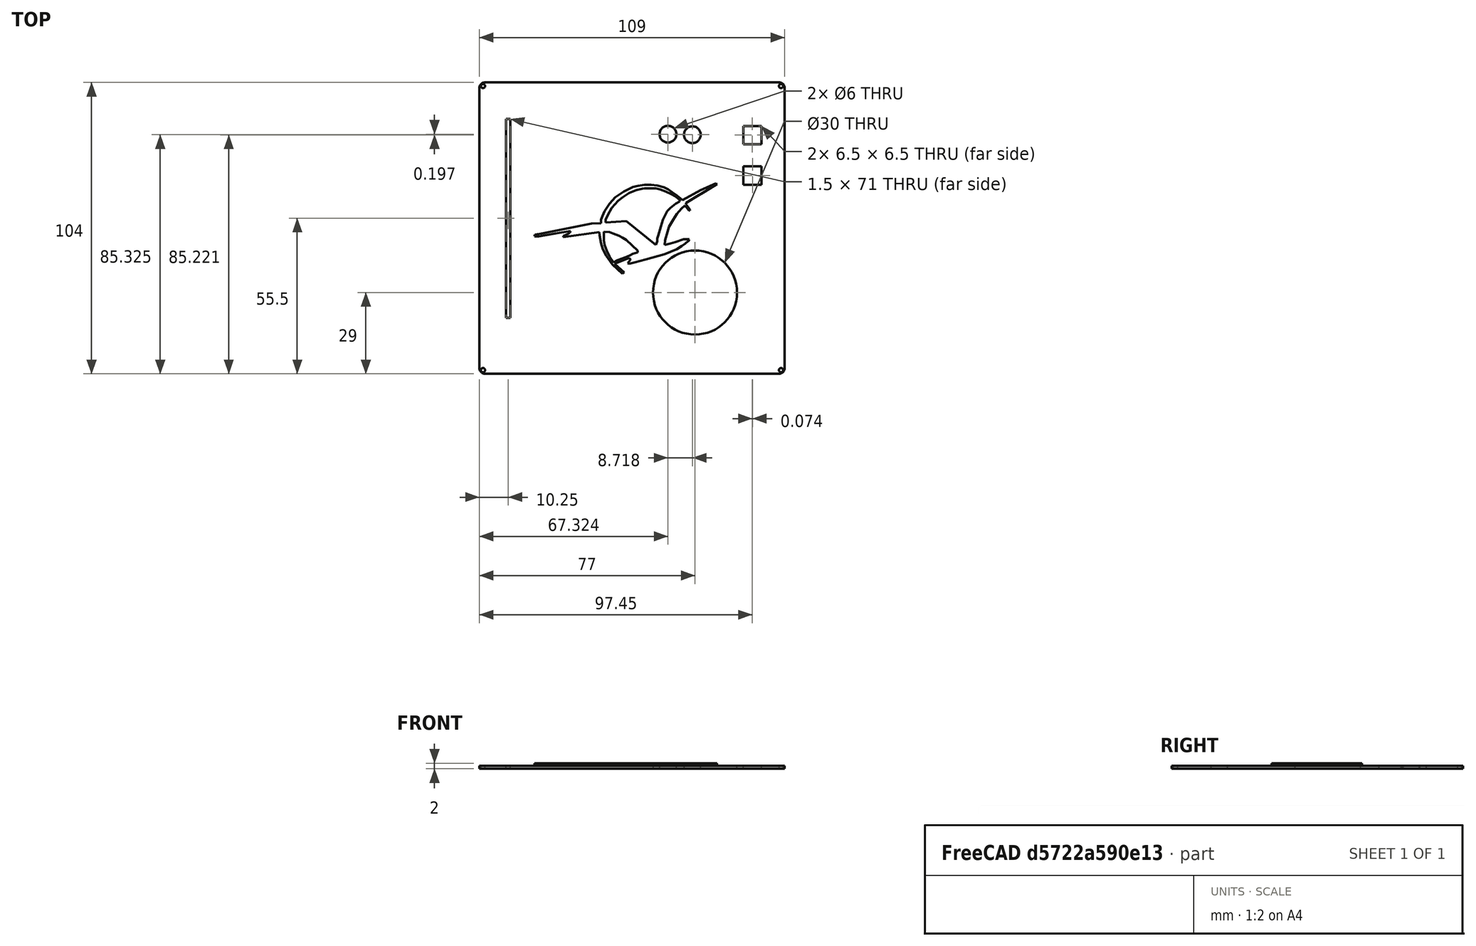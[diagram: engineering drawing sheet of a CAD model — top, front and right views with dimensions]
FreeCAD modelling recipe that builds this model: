
FCSTD DOCUMENT  (FreeCAD 2024.1R35694 (Git))
Label: kryshka
License: All rights reserved
LicenseURL: https://en.wikipedia.org/wiki/All_rights_reserved
objects: Sketcher::SketchObject×3, PartDesign::Pad×2, Image::ImagePlane×1, PartDesign::Body×1, App::MeasureDistance×1
note: 8 computed .brp shape members not serialized (recipe doc carries the construction recipe); baked Part::Feature solids carry a one-line shape summary decoded from their .brp

FEATURE [Sketcher::SketchObject] Sketch
  FullyConstrained = false
  MapMode = 5
  Support = -> [XY_Plane]
  sketch-geometry (29):
    g0: LineSegment StartX=-54.5 StartY=50 StartZ=0 EndX=-54.5 EndY=-50 EndZ=0
    g1: LineSegment StartX=-52.5 StartY=-52 StartZ=0 EndX=52.5 EndY=-52 EndZ=0
    g2: LineSegment StartX=54.5 StartY=-50 StartZ=0 EndX=54.5 EndY=50 EndZ=0
    g3: LineSegment StartX=52.5 StartY=52 StartZ=0 EndX=-52.5 EndY=52 EndZ=0
    g4: ArcOfCircle CenterX=-52.5 CenterY=50 CenterZ=0 NormalX=0 NormalY=0 NormalZ=1 AngleXU=0 Radius=2 StartAngle=1.5708 EndAngle=3.14159
    g5: ArcOfCircle CenterX=-52.5 CenterY=-50 CenterZ=0 NormalX=0 NormalY=0 NormalZ=1 AngleXU=0 Radius=2 StartAngle=3.14159 EndAngle=4.71239
    g6: ArcOfCircle CenterX=52.5 CenterY=-50 CenterZ=0 NormalX=0 NormalY=0 NormalZ=1 AngleXU=0 Radius=2 StartAngle=4.71239 EndAngle=6.28319
    g7: ArcOfCircle CenterX=52.5 CenterY=50 CenterZ=0 NormalX=0 NormalY=0 NormalZ=1 AngleXU=0 Radius=2 StartAngle=-1.8e-15 EndAngle=1.5708
    g8: GeomPoint X=-54.5 Y=52 Z=0
    g9: GeomPoint X=54.5 Y=-52 Z=0
    g10: Circle CenterX=-53.2 CenterY=50.7 CenterZ=0 NormalX=0 NormalY=0 NormalZ=1 AngleXU=0 Radius=0.75
    g11: Circle CenterX=-53.2 CenterY=-50.7 CenterZ=0 NormalX=0 NormalY=0 NormalZ=1 AngleXU=0 Radius=0.75
    g12: Circle CenterX=53.2 CenterY=-50.7 CenterZ=0 NormalX=0 NormalY=0 NormalZ=1 AngleXU=0 Radius=0.75
    g13: Circle CenterX=53.2 CenterY=50.7 CenterZ=0 NormalX=0 NormalY=0 NormalZ=1 AngleXU=0 Radius=0.75
    g14: LineSegment StartX=-45 StartY=39 StartZ=0 EndX=-45 EndY=-32 EndZ=0
    g15: LineSegment StartX=-45 StartY=-32 StartZ=0 EndX=-43.5 EndY=-32 EndZ=0
    g16: LineSegment StartX=-43.5 StartY=-32 StartZ=0 EndX=-43.5 EndY=39 EndZ=0
    g17: LineSegment StartX=-43.5 StartY=39 StartZ=0 EndX=-45 EndY=39 EndZ=0
    g18: Circle CenterX=22.5 CenterY=-23 CenterZ=0 NormalX=0 NormalY=0 NormalZ=1 AngleXU=0 Radius=15
    g19: Circle CenterX=12.8244 CenterY=33.5216 CenterZ=0 NormalX=0 NormalY=0 NormalZ=1 AngleXU=0 Radius=3
    g20: Circle CenterX=21.5427 CenterY=33.3249 CenterZ=0 NormalX=0 NormalY=0 NormalZ=1 AngleXU=0 Radius=3
    g21: LineSegment StartX=39.7743 StartY=22.006 StartZ=0 EndX=39.7743 EndY=15.506 EndZ=0
    g22: LineSegment StartX=39.7743 StartY=15.506 StartZ=0 EndX=46.2743 EndY=15.506 EndZ=0
    g23: LineSegment StartX=46.2743 StartY=15.506 StartZ=0 EndX=46.2743 EndY=22.006 EndZ=0
    g24: LineSegment StartX=46.2743 StartY=22.006 StartZ=0 EndX=39.7743 EndY=22.006 EndZ=0
    g25: LineSegment StartX=39.7003 StartY=36.4714 StartZ=0 EndX=39.7003 EndY=29.9714 EndZ=0
    g26: LineSegment StartX=39.7003 StartY=29.9714 StartZ=0 EndX=46.2003 EndY=29.9714 EndZ=0
    g27: LineSegment StartX=46.2003 StartY=29.9714 StartZ=0 EndX=46.2003 EndY=36.4714 EndZ=0
    g28: LineSegment StartX=46.2003 StartY=36.4714 StartZ=0 EndX=39.7003 EndY=36.4714 EndZ=0
  constraints (72):
    c: Tangent(g0,g4) = -1.5708
    c: Tangent(g0,g5) = -1.5708
    c: Tangent(g1,g5) = -1.5708
    c: Tangent(g1,g6) = -1.5708
    c: Tangent(g2,g6) = -1.5708
    c: Tangent(g2,g7) = -1.5708
    c: Tangent(g3,g7) = -1.5708
    c: Tangent(g3,g4) = -1.5708
    c: Vertical(g0)
    c: Vertical(g2)
    c: Horizontal(g1)
    c: Horizontal(g3)
    c: Equal(g4,g5)
    c: Equal(g5,g6)
    c: Equal(g6,g7)
    c: PointOnObject(g8,g0)
    c: PointOnObject(g8,g3)
    c: PointOnObject(g9,g1)
    c: PointOnObject(g9,g2)
    c: Distance(g0,g2) = 109
    c: Distance(g1,g3) = 104
    c: Radius(g5) = 2
    c: Symmetric(g8,g9,g-1)
    c: Radius(g10) = 0.75
    c: DistanceY(g4,g10) = 0.7
    c: DistanceX(g10,g4) = 0.7
    c: Radius(g11) = 0.75
    c: DistanceX(g11,g5) = 0.7
    c: DistanceY(g11,g5) = 0.7
    c: Radius(g12) = 0.75
    c: DistanceY(g12,g6) = 0.7
    c: DistanceX(g6,g12) = 0.7
    c: Radius(g13) = 0.75
    c: DistanceY(g7,g13) = 0.7
    c: DistanceX(g7,g13) = 0.7
    c: Coincident(g14,g15)
    c: Coincident(g15,g16)
    c: Coincident(g16,g17)
    c: Coincident(g17,g14)
    c: Vertical(g14)
    c: Vertical(g16)
    c: Horizontal(g15)
    c: Horizontal(g17)
    c: Distance(g14,g16) = 1.5
    c: Distance(g15,g17) = 71
    c: DistanceX(g0,g14) = 9.5
    c: DistanceY(g14,g3) = 13
    c: Radius(g18) = 15
    c: DistanceX(g18,g2) = 32
    c: DistanceY(g9,g18) = 29
    c: Radius(g19) = 3
    c: Radius(g20) = 3
    c: Coincident(g21,g22)
    c: Coincident(g22,g23)
    c: Coincident(g23,g24)
    c: Coincident(g24,g21)
    c: Vertical(g21)
    c: Vertical(g23)
    c: Horizontal(g22)
    c: Horizontal(g24)
    c: Distance(g21,g23) = 6.5
    c: Distance(g22,g24) = 6.5
    c: Coincident(g25,g26)
    c: Coincident(g26,g27)
    c: Coincident(g27,g28)
    c: Coincident(g28,g25)
    c: Vertical(g25)
    c: Vertical(g27)
    c: Horizontal(g26)
    c: Horizontal(g28)
    c: Distance(g25,g27) = 6.5
    c: Distance(g26,g28) = 6.5
FEATURE [PartDesign::Pad] Pad
  Direction = (0,0,1)
  Length = 1
  Length2 = 10
  Profile = -> Sketch
  ReferenceAxis = -> Sketch [N_Axis]
  Refine = true
  Type = 0
FEATURE [Sketcher::SketchObject] Sketch001
  FullyConstrained = true
  MapMode = 5
  Placement = pos=(39.7003,0,0) rot=(0.57735,0.57735,0.57735;2.0944rad)
  Support = -> [Pad]
FEATURE [Image::ImagePlane] rt
  XSize = 78.3069
  YSize = 44.9735
FEATURE [Sketcher::SketchObject] Sketch002
  FullyConstrained = false
  MapMode = 5
  Support = -> [XY_Plane]
  sketch-geometry (121):
    g0: LineSegment StartX=-34.7733 StartY=-3 StartZ=0 EndX=-34.7499 EndY=-2.33713 EndZ=0
    g1: LineSegment StartX=-34.7499 StartY=-2.33713 StartZ=0 EndX=-32.2664 EndY=-2 EndZ=0
    g2: LineSegment StartX=-32.2664 StartY=-2 StartZ=0 EndX=-14.5219 EndY=1.61821 EndZ=0
    g3: LineSegment StartX=-14.5219 StartY=1.61821 StartZ=0 EndX=-11 EndY=1.79215 EndZ=0
    g4: LineSegment StartX=-11 StartY=1.79215 StartZ=0 EndX=-11 EndY=3 EndZ=0
    g5: LineSegment StartX=-11 StartY=3 StartZ=0 EndX=-10.5907 EndY=4.26218 EndZ=0
    g6: LineSegment StartX=-10.5907 StartY=4.26218 StartZ=0 EndX=-9.75577 EndY=6 EndZ=0
    g7: LineSegment StartX=-9.75577 StartY=6 StartZ=0 EndX=-8 EndY=8.77106 EndZ=0
    g8: LineSegment StartX=-8 StartY=8.77106 StartZ=0 EndX=-6 EndY=11 EndZ=0
    g9: LineSegment StartX=-6 StartY=11 StartZ=0 EndX=-3 EndY=13 EndZ=0
    g10: LineSegment StartX=-3 StartY=13 StartZ=0 EndX=0.374559 EndY=14.714 EndZ=0
    g11: LineSegment StartX=0.374559 StartY=14.714 StartZ=0 EndX=2.2 EndY=15.1 EndZ=0
    g12: LineSegment StartX=2.2 StartY=15.1 StartZ=0 EndX=4.45571 EndY=15.4013 EndZ=0
    g13: LineSegment StartX=4.45571 StartY=15.4013 StartZ=0 EndX=6.78659 EndY=15.4013 EndZ=0
    g14: LineSegment StartX=6.78659 StartY=15.4013 StartZ=0 EndX=9 EndY=15.2221 EndZ=0
    g15: LineSegment StartX=9 StartY=15.2221 StartZ=0 EndX=11.4375 EndY=14.5437 EndZ=0
    g16: LineSegment StartX=11.4375 StartY=14.5437 StartZ=0 EndX=13 EndY=13.7546 EndZ=0
    g17: LineSegment StartX=13 StartY=13.7546 StartZ=0 EndX=14.3855 EndY=12.7719 EndZ=0
    g18: LineSegment StartX=14.3855 StartY=12.7719 StartZ=0 EndX=16 EndY=11.6183 EndZ=0
    g19: LineSegment StartX=16 StartY=11.6183 StartZ=0 EndX=18 EndY=10 EndZ=0
    g20: LineSegment StartX=18 StartY=10 StartZ=0 EndX=24.5463 EndY=13.5843 EndZ=0
    g21: LineSegment StartX=24.5463 StartY=13.5843 StartZ=0 EndX=30 EndY=16 EndZ=0
    g22: LineSegment StartX=30 StartY=16 StartZ=0 EndX=30.2896 EndY=15.7063 EndZ=0
    g23: LineSegment StartX=30.2896 StartY=15.7063 StartZ=0 EndX=26 EndY=13 EndZ=0
    g24: LineSegment StartX=26 StartY=13 StartZ=0 EndX=22.6257 EndY=11 EndZ=0
    g25: LineSegment StartX=22.6257 StartY=11 StartZ=0 EndX=19.3042 EndY=9 EndZ=0
    g26: LineSegment StartX=19.3042 StartY=9 StartZ=0 EndX=19.3042 EndY=8.49227 EndZ=0
    g27: LineSegment StartX=19.3042 StartY=8.49227 StartZ=0 EndX=20.6795 EndY=6.52009 EndZ=0
    g28: LineSegment StartX=20.6795 StartY=6.52009 StartZ=0 EndX=20.7055 EndY=6.2606 EndZ=0
    g29: LineSegment StartX=20.7055 StartY=6.2606 StartZ=0 EndX=20.2903 EndY=6.3125 EndZ=0
    g30: LineSegment StartX=20.2903 StartY=6.3125 StartZ=0 EndX=18.8598 EndY=8.1 EndZ=0
    g31: LineSegment StartX=18.8598 StartY=8.1 StartZ=0 EndX=17.6926 EndY=7 EndZ=0
    g32: LineSegment StartX=17.6926 StartY=7 StartZ=0 EndX=16 EndY=5 EndZ=0
    g33: LineSegment StartX=16 StartY=5 StartZ=0 EndX=14.7084 EndY=3 EndZ=0
    g34: LineSegment StartX=14.7084 StartY=3 StartZ=0 EndX=13.2552 EndY=0.51859 EndZ=0
    g35: LineSegment StartX=13.2552 StartY=0.51859 StartZ=0 EndX=12.6673 EndY=-1.26122 EndZ=0
    g36: LineSegment StartX=12.6673 StartY=-1.26122 StartZ=0 EndX=11.7962 EndY=-4.36312 EndZ=0
    g37: LineSegment StartX=11.7962 StartY=-4.36312 StartZ=0 EndX=11.6475 EndY=-6 EndZ=0
    g38: LineSegment StartX=11.6475 StartY=-6 StartZ=0 EndX=13.7508 EndY=-5.55289 EndZ=0
    g39: LineSegment StartX=13.7508 StartY=-5.55289 StartZ=0 EndX=15.4292 EndY=-5 EndZ=0
    g40: LineSegment StartX=15.4292 StartY=-5 StartZ=0 EndX=18.4249 EndY=-4 EndZ=0
    g41: LineSegment StartX=18.4249 StartY=-4 StartZ=0 EndX=20.4433 EndY=-4 EndZ=0
    g42: LineSegment StartX=20.4433 StartY=-4 StartZ=0 EndX=20 EndY=-4.55433 EndZ=0
    g43: LineSegment StartX=20 StartY=-4.55433 StartZ=0 EndX=19 EndY=-5.4679 EndZ=0
    g44: LineSegment StartX=19 StartY=-5.4679 StartZ=0 EndX=17.7932 EndY=-6.43095 EndZ=0
    g45: LineSegment StartX=17.7932 StartY=-6.43095 StartZ=0 EndX=16 EndY=-7.47463 EndZ=0
    g46: LineSegment StartX=16 StartY=-7.47463 StartZ=0 EndX=11.6181 EndY=-9.30106 EndZ=0
    g47: LineSegment StartX=11.6181 StartY=-9.30106 StartZ=0 EndX=4.78203 EndY=-11.2493 EndZ=0
    g48: LineSegment StartX=4.78203 StartY=-11.2493 StartZ=0 EndX=1 EndY=-12.2364 EndZ=0
    g49: LineSegment StartX=1 StartY=-12.2364 StartZ=0 EndX=-1 EndY=-12.793 EndZ=0
    g50: LineSegment StartX=-1 StartY=-12.793 StartZ=0 EndX=-1.5477 EndY=-12.4625 EndZ=0
    g51: LineSegment StartX=-1.5477 StartY=-12.4625 StartZ=0 EndX=-0.623532 EndY=-11.4271 EndZ=0
    g52: LineSegment StartX=-0.623532 StartY=-11.4271 StartZ=0 EndX=-0.6 EndY=-10.9 EndZ=0
    g53: LineSegment StartX=-0.6 StartY=-10.9 StartZ=0 EndX=-1 EndY=-10.7451 EndZ=0
    g54: LineSegment StartX=-1 StartY=-10.7451 StartZ=0 EndX=-1.8 EndY=-10.9252 EndZ=0
    g55: LineSegment StartX=-1.8 StartY=-10.9252 StartZ=0 EndX=-6.24816 EndY=-12.6962 EndZ=0
    g56: LineSegment StartX=-6.24816 StartY=-12.6962 StartZ=0 EndX=-2.83824 EndY=-15.8401 EndZ=0
    g57: LineSegment StartX=-2.83824 StartY=-15.8401 StartZ=0 EndX=-3.4 EndY=-16.2562 EndZ=0
    g58: LineSegment StartX=-3.4 StartY=-16.2562 StartZ=0 EndX=-7 EndY=-13 EndZ=0
    g59: LineSegment StartX=-7 StartY=-13 StartZ=0 EndX=-9.22125 EndY=-10 EndZ=0
    g60: LineSegment StartX=-9.22125 StartY=-10 StartZ=0 EndX=-10.3943 EndY=-7.51802 EndZ=0
    g61: LineSegment StartX=-10.3943 StartY=-7.51802 StartZ=0 EndX=-11 EndY=-5.35344 EndZ=0
    g62: LineSegment StartX=-11 StartY=-5.35344 StartZ=0 EndX=-11.5843 EndY=-2.59002 EndZ=0
    g63: LineSegment StartX=-11.5843 StartY=-2.59002 StartZ=0 EndX=-11.666 EndY=-1.38904 EndZ=0
    g64: LineSegment StartX=-11.666 StartY=-1.38904 StartZ=0 EndX=-24.5219 EndY=-3.23781 EndZ=0
    g65: LineSegment StartX=-24.5219 StartY=-3.23781 StartZ=0 EndX=-24.5503 EndY=-2.78208 EndZ=0
    g66: LineSegment StartX=-24.5503 StartY=-2.78208 StartZ=0 EndX=-23.4253 EndY=-2.36907 EndZ=0
    g67: LineSegment StartX=-23.4253 StartY=-2.36907 StartZ=0 EndX=-22.2147 EndY=-1.65699 EndZ=0
    g68: LineSegment StartX=-22.2147 StartY=-1.65699 StartZ=0 EndX=-22 EndY=-1 EndZ=0
    g69: LineSegment StartX=-22 StartY=-1 StartZ=0 EndX=-27.4592 EndY=-2 EndZ=0
    g70: LineSegment StartX=-27.4592 StartY=-2 StartZ=0 EndX=-33.3013 EndY=-3 EndZ=0
    g71: LineSegment StartX=-33.3013 StartY=-3 StartZ=0 EndX=-34.7733 EndY=-3 EndZ=0
    g72: LineSegment StartX=-10 StartY=-1.33522 StartZ=0 EndX=-8 EndY=-1.40755 EndZ=0
    g73: LineSegment StartX=-8 StartY=-1.40755 StartZ=0 EndX=-6.69036 EndY=-2 EndZ=0
    g74: LineSegment StartX=-6.69036 StartY=-2 StartZ=0 EndX=-4.76445 EndY=-2.73196 EndZ=0
    g75: LineSegment StartX=-4.76445 StartY=-2.73196 StartZ=0 EndX=-3.31128 EndY=-3.51045 EndZ=0
    g76: LineSegment StartX=-3.31128 StartY=-3.51045 StartZ=0 EndX=-2 EndY=-4.28894 EndZ=0
    g77: LineSegment StartX=-2 StartY=-4.28894 StartZ=0 EndX=2 EndY=-8 EndZ=0
    g78: LineSegment StartX=2 StartY=-8 StartZ=0 EndX=2 EndY=-8.46683 EndZ=0
    g79: LineSegment StartX=2 StartY=-8.46683 StartZ=0 EndX=2 EndY=-8.70038 EndZ=0
    g80: LineSegment StartX=2 StartY=-8.70038 StartZ=0 EndX=0.29573 EndY=-9.24532 EndZ=0
    g81: LineSegment StartX=0.29573 StartY=-9.24532 StartZ=0 EndX=-0.664407 EndY=-9.68647 EndZ=0
    g82: LineSegment StartX=-0.664407 StartY=-9.68647 StartZ=0 EndX=-2 EndY=-10.2833 EndZ=0
    g83: LineSegment StartX=-2 StartY=-10.2833 StartZ=0 EndX=-5.2575 EndY=-11.5289 EndZ=0
    g84: LineSegment StartX=-5.2575 StartY=-11.5289 StartZ=0 EndX=-6.63321 EndY=-12.2534 EndZ=0
    g85: LineSegment StartX=-6.63321 StartY=-12.2534 StartZ=0 EndX=-8 EndY=-10.2487 EndZ=0
    g86: LineSegment StartX=-8 StartY=-10.2487 StartZ=0 EndX=-9 EndY=-8 EndZ=0
    g87: LineSegment StartX=-9 StartY=-8 StartZ=0 EndX=-9.78238 EndY=-6 EndZ=0
    g88: LineSegment StartX=-9.78238 StartY=-6 StartZ=0 EndX=-10 EndY=-4.41003 EndZ=0
    g89: LineSegment StartX=-10 StartY=-4.41003 StartZ=0 EndX=-10 EndY=-1.33522 EndZ=0
    g90: LineSegment StartX=-9.47686 StartY=2 StartZ=0 EndX=-9.47686 EndY=3 EndZ=0
    g91: LineSegment StartX=-9.47686 StartY=3 StartZ=0 EndX=-8.70385 EndY=4.62033 EndZ=0
    g92: LineSegment StartX=-8.70385 StartY=4.62033 StartZ=0 EndX=-7.23514 EndY=7.23705 EndZ=0
    g93: LineSegment StartX=-7.23514 StartY=7.23705 StartZ=0 EndX=-5 EndY=9.69777 EndZ=0
    g94: LineSegment StartX=-5 StartY=9.69777 StartZ=0 EndX=-3.36412 EndY=11 EndZ=0
    g95: LineSegment StartX=-3.36412 StartY=11 StartZ=0 EndX=-1 EndY=12.5331 EndZ=0
    g96: LineSegment StartX=-1 StartY=12.5331 StartZ=0 EndX=1.56882 EndY=13.5121 EndZ=0
    g97: LineSegment StartX=1.56882 StartY=13.5121 StartZ=0 EndX=3.64807 EndY=14 EndZ=0
    g98: LineSegment StartX=3.64807 StartY=14 StartZ=0 EndX=4.4 EndY=14.1486 EndZ=0
    g99: LineSegment StartX=4.4 StartY=14.1486 StartZ=0 EndX=7.4 EndY=14.1486 EndZ=0
    g100: LineSegment StartX=7.4 StartY=14.1486 StartZ=0 EndX=8.46425 EndY=14.1486 EndZ=0
    g101: LineSegment StartX=8.46425 StartY=14.1486 StartZ=0 EndX=10 EndY=13.748 EndZ=0
    g102: LineSegment StartX=10 StartY=13.748 StartZ=0 EndX=11 EndY=13.4692 EndZ=0
    g103: LineSegment StartX=11 StartY=13.4692 StartZ=0 EndX=12.048 EndY=13.1 EndZ=0
    g104: LineSegment StartX=12.048 StartY=13.1 StartZ=0 EndX=13.9539 EndY=12.1727 EndZ=0
    g105: LineSegment StartX=13.9539 StartY=12.1727 StartZ=0 EndX=15.3 EndY=11.3467 EndZ=0
    g106: LineSegment StartX=15.3 StartY=11.3467 StartZ=0 EndX=17 EndY=10.1705 EndZ=0
    g107: LineSegment StartX=17 StartY=10.1705 StartZ=0 EndX=17.033 EndY=9.44742 EndZ=0
    g108: LineSegment StartX=17.033 StartY=9.44742 StartZ=0 EndX=15.5751 EndY=8.67393 EndZ=0
    g109: LineSegment StartX=15.5751 StartY=8.67393 StartZ=0 EndX=13.727 EndY=7.2256 EndZ=0
    g110: LineSegment StartX=13.727 StartY=7.2256 StartZ=0 EndX=13 EndY=6.482 EndZ=0
    g111: LineSegment StartX=13 StartY=6.482 StartZ=0 EndX=12.6009 EndY=6 EndZ=0
    g112: LineSegment StartX=12.6009 StartY=6 StartZ=0 EndX=12 EndY=5 EndZ=0
    g113: LineSegment StartX=12 StartY=5 StartZ=0 EndX=11 EndY=3 EndZ=0
    g114: LineSegment StartX=11 StartY=3 StartZ=0 EndX=10.2202 EndY=0.508264 EndZ=0
    g115: LineSegment StartX=10.2202 StartY=0.508264 StartZ=0 EndX=9.36427 EndY=-2.641 EndZ=0
    g116: LineSegment StartX=9.36427 StartY=-2.641 StartZ=0 EndX=9 EndY=-3.78279 EndZ=0
    g117: LineSegment StartX=9 StartY=-3.78279 StartZ=0 EndX=9 EndY=-4.71698 EndZ=0
    g118: LineSegment StartX=9 StartY=-4.71698 StartZ=0 EndX=8.54919 EndY=-6 EndZ=0
    g119: LineSegment StartX=8.54919 StartY=-6 StartZ=0 EndX=-2 EndY=2.54303 EndZ=0
    g120: LineSegment StartX=-2 StartY=2.54303 StartZ=0 EndX=-9.47686 EndY=2 EndZ=0
  constraints (133):
    c: Coincident(g0,g1)
    c: Coincident(g1,g2)
    c: Coincident(g2,g3)
    c: Coincident(g3,g4)
    c: Vertical(g4)
    c: Coincident(g4,g5)
    c: Coincident(g5,g6)
    c: Coincident(g6,g7)
    c: Coincident(g7,g8)
    c: Coincident(g8,g9)
    c: Coincident(g9,g10)
    c: Coincident(g10,g11)
    c: Coincident(g11,g12)
    c: Coincident(g12,g13)
    c: Horizontal(g13)
    c: Coincident(g13,g14)
    c: Coincident(g14,g15)
    c: Coincident(g15,g16)
    c: Coincident(g16,g17)
    c: Coincident(g17,g18)
    c: Coincident(g18,g19)
    c: Coincident(g19,g20)
    c: Coincident(g20,g21)
    c: Coincident(g21,g22)
    c: Coincident(g22,g23)
    c: Coincident(g23,g24)
    c: Coincident(g24,g25)
    c: Coincident(g25,g26)
    c: Vertical(g26)
    c: Coincident(g26,g27)
    c: Coincident(g27,g28)
    c: Coincident(g28,g29)
    c: Coincident(g29,g30)
    c: Coincident(g30,g31)
    c: Coincident(g31,g32)
    c: Coincident(g32,g33)
    c: Coincident(g33,g34)
    c: Coincident(g34,g35)
    c: Coincident(g35,g36)
    c: Coincident(g36,g37)
    c: Coincident(g37,g38)
    c: Coincident(g38,g39)
    c: Coincident(g39,g40)
    c: Coincident(g40,g41)
    c: Horizontal(g41)
    c: Coincident(g41,g42)
    c: Coincident(g42,g43)
    c: Coincident(g43,g44)
    c: Coincident(g44,g45)
    c: Coincident(g45,g46)
    c: Coincident(g46,g47)
    c: Coincident(g47,g48)
    c: Coincident(g48,g49)
    c: Coincident(g49,g50)
    c: Coincident(g50,g51)
    c: Coincident(g51,g52)
    c: Coincident(g52,g53)
    c: Coincident(g53,g54)
    c: Coincident(g54,g55)
    c: Coincident(g55,g56)
    c: Coincident(g56,g57)
    c: Coincident(g57,g58)
    c: Coincident(g58,g59)
    c: Coincident(g59,g60)
    c: Coincident(g60,g61)
    c: Coincident(g61,g62)
    c: Coincident(g62,g63)
    c: Coincident(g63,g64)
    c: Coincident(g64,g65)
    c: Coincident(g65,g66)
    c: Coincident(g66,g67)
    c: Coincident(g67,g68)
    c: Coincident(g68,g69)
    c: Coincident(g69,g70)
    c: Coincident(g70,g71)
    c: Coincident(g71,g0)
    c: Horizontal(g71)
    c: Coincident(g72,g73)
    c: Coincident(g73,g74)
    c: Coincident(g74,g75)
    c: Coincident(g75,g76)
    c: Coincident(g76,g77)
    c: Coincident(g77,g78)
    c: Vertical(g78)
    c: Coincident(g78,g79)
    c: Vertical(g79)
    c: Coincident(g79,g80)
    c: Coincident(g80,g81)
    c: Coincident(g81,g82)
    c: Coincident(g82,g83)
    c: Coincident(g83,g84)
    c: Coincident(g84,g85)
    c: Coincident(g85,g86)
    c: Coincident(g86,g87)
    c: Coincident(g87,g88)
    c: Coincident(g88,g89)
    c: Coincident(g89,g72)
    c: Vertical(g89)
    c: Vertical(g90)
    c: Coincident(g90,g91)
    c: Coincident(g91,g92)
    c: Coincident(g92,g93)
    c: Coincident(g93,g94)
    c: Coincident(g94,g95)
    c: Coincident(g95,g96)
    c: Coincident(g96,g97)
    c: Coincident(g97,g98)
    c: Coincident(g98,g99)
    c: Horizontal(g99)
    c: Coincident(g99,g100)
    c: Horizontal(g100)
    c: Coincident(g100,g101)
    c: Coincident(g101,g102)
    c: Coincident(g102,g103)
    c: Coincident(g103,g104)
    c: Coincident(g104,g105)
    c: Coincident(g105,g106)
    c: Coincident(g106,g107)
    c: Coincident(g107,g108)
    c: Coincident(g108,g109)
    c: Coincident(g109,g110)
    c: Coincident(g110,g111)
    c: Coincident(g111,g112)
    c: Coincident(g112,g113)
    c: Coincident(g113,g114)
    c: Coincident(g114,g115)
    c: Coincident(g115,g116)
    c: Coincident(g116,g117)
    c: Vertical(g117)
    c: Coincident(g117,g118)
    c: Coincident(g118,g119)
    c: Coincident(g119,g120)
    c: Coincident(g120,g90)
FEATURE [PartDesign::Pad] Pad001
  BaseFeature = -> Pad
  Direction = (0,0,1)
  Length = 2
  Length2 = 10
  Profile = -> Sketch002
  ReferenceAxis = -> Sketch002 [N_Axis]
  Refine = true
  Type = 0
FEATURE [PartDesign::Body] Body
  Group = -> [Sketch,Pad,Sketch001,Sketch002,Pad001]
  Origin = -> Origin
  Tip = -> Pad001
FEATURE [App::MeasureDistance] Distance  label="Distance: 0,859 mm"
  Distance = 0.859233
  P1 = (13.2794,-8.69899,1)
  P2 = (13.8435,-9.34707,1)
